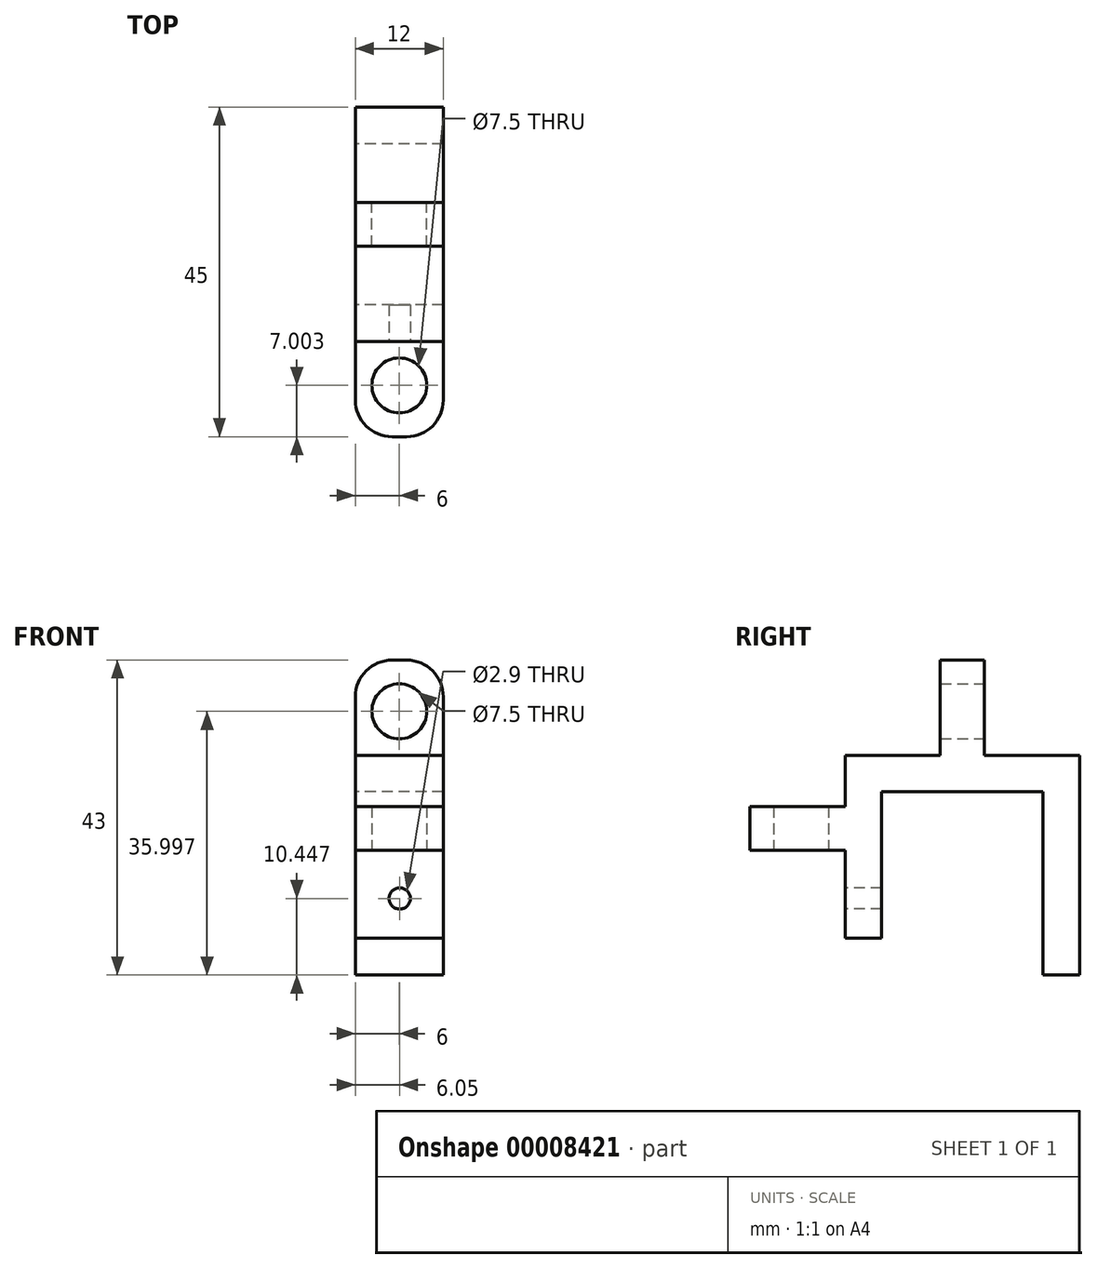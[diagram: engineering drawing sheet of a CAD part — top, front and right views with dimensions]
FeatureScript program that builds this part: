
annotation { "Feature Type Name" : "Feature", "Feature Type Description" : "" }
export const myFeature = defineFeature(function(context is Context, id is Id, definition is map)
    precondition{}
    {
        {
            var Q0;
            Q0=qCreatedBy(makeId("Right.planeOp"),FACE);
            var sketch = newSketch(context, id + "F0", { "sketchPlane" : qUnion([Q0])});
            skLineSegment(sketch, "E0", {"start": v(10.72, 31.3) * mm, "end": v(10.72, 6.3) * mm});
            skLineSegment(sketch, "E1", {"start": v(10.72, 31.3) * mm, "end": v(-11.28, 31.3) * mm});
            skLineSegment(sketch, "E2", {"start": v(-11.28, 31.3) * mm, "end": v(-11.28, 11.3) * mm});
            skLineSegment(sketch, "E3", {"start": v(-11.28, 11.3) * mm, "end": v(-16.28, 11.3) * mm});
            skLineSegment(sketch, "E4", {"start": v(-16.28, 11.3) * mm, "end": v(-16.28, 36.3) * mm});
            skLineSegment(sketch, "E5", {"start": v(-16.28, 36.3) * mm, "end": v(15.72, 36.3) * mm});
            skLineSegment(sketch, "E6", {"start": v(15.72, 36.3) * mm, "end": v(15.72, 6.3) * mm});
            skLineSegment(sketch, "E7", {"start": v(15.72, 6.3) * mm, "end": v(10.72, 6.3) * mm});
            skSolve(sketch);
        }
        {
            var Q0;
            Q0 = qSketchRegion(id + "F0", true);
            extrude(context, id + "F1", {"entities" : qUnion([Q0]), "depth" : 12 * mm});
        }
        {
            var Q0;
            Q0=makeQuery(id+"F1.opExtrude","SWEPT_FACE",FACE,{"disambiguationData":[OSD([sQuery(id+"F0.wireOp",EDGE,"E4")])]});
            var sketch = newSketch(context, id + "F2", { "sketchPlane" : qUnion([Q0])});
            skCircle(sketch, "E8", {"center": v(6.05, 16.76) * mm, "radius": 1.45 * mm});
            skSolve(sketch);
        }
        {
            var Q0;
            Q0 = qSketchRegion(id + "F2", true);
            extrude(context, id + "F3", {"entities" : qUnion([Q0]), "operationType" : NewBodyOperationType.REMOVE, "oppositeDirection" : true, "depth" : 5 * mm});
        }
        {
            var Q0;
            Q0=makeQuery(id+"F1.opExtrude","SWEPT_FACE",FACE,{"disambiguationData":[OSD([sQuery(id+"F0.wireOp",EDGE,"E5")])]});
            var sketch = newSketch(context, id + "F4", { "sketchPlane" : qUnion([Q0])});
            skLineSegment(sketch, "E9", {"start": v(0, 2.72) * mm, "end": v(12, 2.72) * mm});
            skLineSegment(sketch, "E10", {"start": v(12, 2.72) * mm, "end": v(12, -3.28) * mm});
            skLineSegment(sketch, "E11", {"start": v(12, -3.28) * mm, "end": v(0, -3.28) * mm});
            skLineSegment(sketch, "E12", {"start": v(0, -3.28) * mm, "end": v(0, 2.72) * mm});
            skSolve(sketch);
        }
        {
            var Q0;
            Q0 = qSketchRegion(id + "F4", true);
            extrude(context, id + "F5", {"entities" : qUnion([Q0]), "operationType" : NewBodyOperationType.ADD, "depth" : 13 * mm});
        }
        {
            var Q0;
            Q0=makeQuery(id+"F5.opExtrude","SWEPT_FACE",FACE,{"disambiguationData":[OSD([sQuery(id+"F4.wireOp",EDGE,"E9")])]});
            var sketch = newSketch(context, id + "F6", { "sketchPlane" : qUnion([Q0])});
            skCircle(sketch, "E13", {"center": v(-6, 42.3) * mm, "radius": 3.75 * mm});
            skSolve(sketch);
        }
        {
            var Q0;
            Q0=makeQuery(id+"F6.imprint","IMPRINT",FACE,{"disambiguationData":[TD([[makeQuery(id+"F6.imprint","IMPRINT",EDGE,{"derivedFrom":sQuery(id+"F6.wireOp",EDGE,"E13")}),1.0]])]});
            extrude(context, id + "F7", {"entities" : qUnion([Q0]), "operationType" : NewBodyOperationType.REMOVE, "oppositeDirection" : true, "depth" : 35 * mm});
        }
        {
            var Q0;
            Q0=makeQuery(id+"F1.opExtrude","SWEPT_FACE",FACE,{"disambiguationData":[OSD([sQuery(id+"F0.wireOp",EDGE,"E4")])]});
            var sketch = newSketch(context, id + "F8", { "sketchPlane" : qUnion([Q0])});
            skLineSegment(sketch, "E14", {"start": v(0, 29.3) * mm, "end": v(12, 29.3) * mm});
            skLineSegment(sketch, "E15", {"start": v(0, 23.3) * mm, "end": v(12, 23.3) * mm});
            skSolve(sketch);
        }
        {
            var Q0;
            {var subQ3=sQuery(id+"F8.wireOp",EDGE,"E14");Q0=makeQuery(id+"F8.imprint","IMPRINT",FACE,{"disambiguationData":[TD([[makeQuery(id+"F8.imprint","IMPRINT",EDGE,{"derivedFrom":subQ3}),-1.0]])]});}
            extrude(context, id + "F9", {"entities" : qUnion([Q0]), "operationType" : NewBodyOperationType.ADD, "depth" : 13 * mm});
        }
        {
            var Q0;
            Q0=makeQuery(id+"F9.opExtrude","SWEPT_FACE",FACE,{"disambiguationData":[OSD([sQuery(id+"F8.wireOp",EDGE,"E15")])]});
            var sketch = newSketch(context, id + "F10", { "sketchPlane" : qUnion([Q0])});
            skCircle(sketch, "E16", {"center": v(6, 22.28) * mm, "radius": 3.75 * mm});
            skSolve(sketch);
        }
        {
            var Q0;
            Q0 = qSketchRegion(id + "F10", true);
            extrude(context, id + "F11", {"entities" : qUnion([Q0]), "operationType" : NewBodyOperationType.REMOVE, "oppositeDirection" : true, "depth" : 25 * mm});
        }
        {
            var Q0;
            Q0=makeQuery(id+"F5.opExtrude","CAP_EDGE",EDGE,{"disambiguationData":[OSD([sQuery(id+"F4.wireOp",EDGE,"E12")])],"isStart":false});
            var Q1;
            {var subQ0=sQuery(id+"F0.wireOp",EDGE,"E4");var subQ1=makeQuery(id+"F1.opExtrude","CAP_EDGE",EDGE,{"disambiguationData":[OSD([subQ0])],"isStart":true});Q1=makeQuery(id+"F9.opExtrude","CAP_EDGE",EDGE,{"disambiguationData":[OSD([subQ0]),TDD([makeQuery(id+"F8.imprint","IMPRINT",EDGE,{"disambiguationData":[TD([[makeQuery(id+"F8.imprint","INTERSECT",VERTEX,{"derivedFrom":[subQ1,sQuery(id+"F8.wireOp",EDGE,"E14")]}),1.0]])],"derivedFrom":subQ1})])],"isStart":false});}
            var Q2;
            {var subQ0=sQuery(id+"F0.wireOp",EDGE,"E4");var subQ1=makeQuery(id+"F1.opExtrude","CAP_EDGE",EDGE,{"disambiguationData":[OSD([subQ0])],"isStart":false});Q2=makeQuery(id+"F9.opExtrude","CAP_EDGE",EDGE,{"disambiguationData":[OSD([subQ0]),TDD([makeQuery(id+"F8.imprint","IMPRINT",EDGE,{"disambiguationData":[TD([[makeQuery(id+"F8.imprint","INTERSECT",VERTEX,{"derivedFrom":[subQ1,sQuery(id+"F8.wireOp",EDGE,"E14")]}),1.0]])],"derivedFrom":subQ1})])],"isStart":false});}
            var Q3;
            Q3=makeQuery(id+"F5.opExtrude","CAP_EDGE",EDGE,{"disambiguationData":[OSD([sQuery(id+"F4.wireOp",EDGE,"E10")])],"isStart":false});
            fillet(context, id + "F12", {"entities" : qUnion([Q0, Q1, Q2, Q3]), "radius" : 5 * mm, "tangentPropagation" : true, "allowEdgeOverflow" : false});
        }
    });
